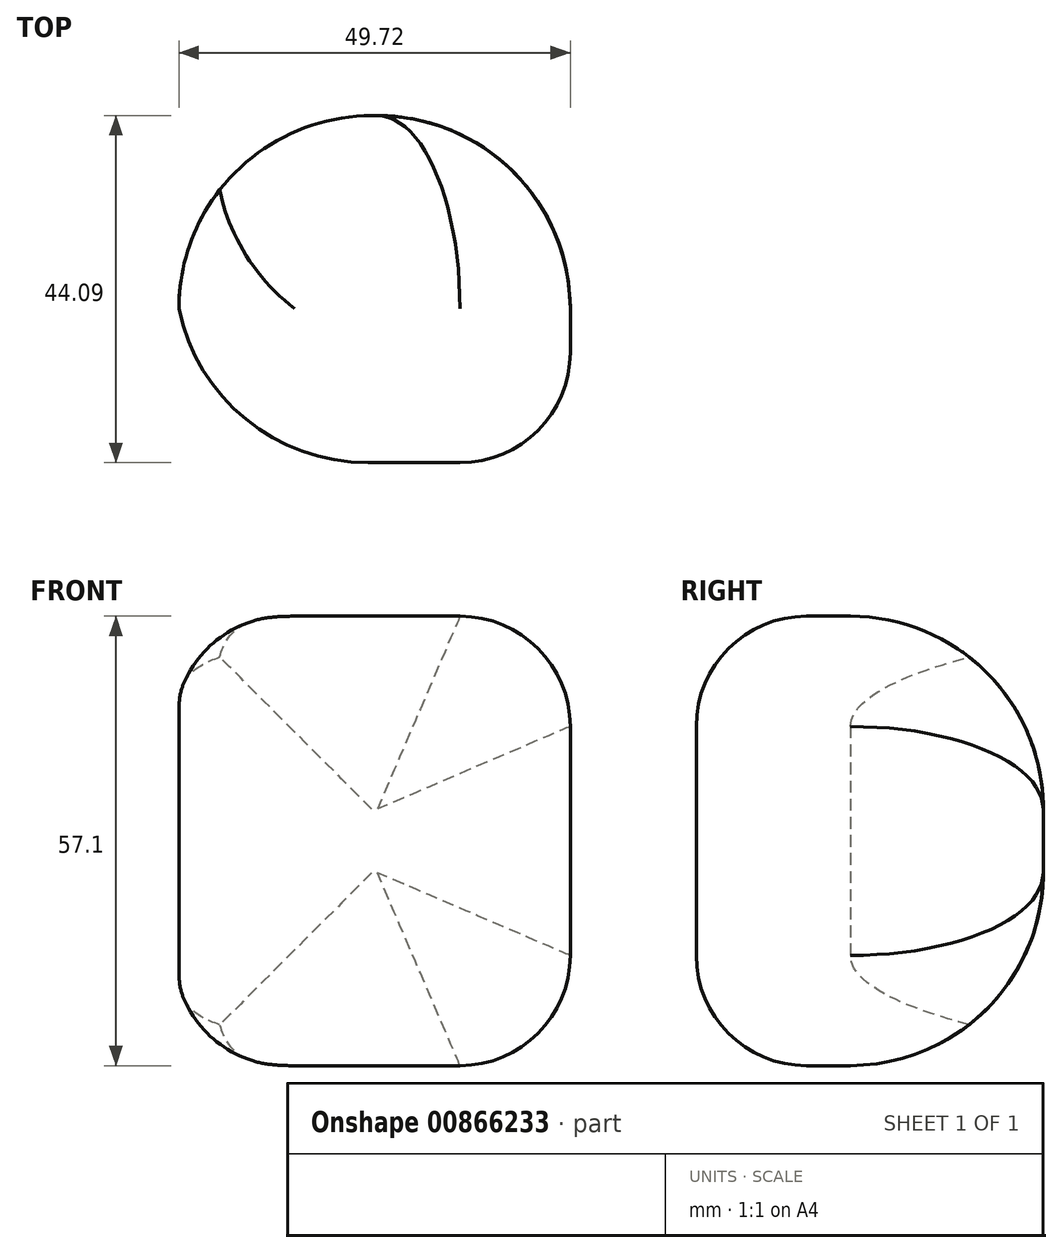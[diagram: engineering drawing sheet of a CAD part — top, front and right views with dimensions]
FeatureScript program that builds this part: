
annotation { "Feature Type Name" : "Feature", "Feature Type Description" : "" }
export const myFeature = defineFeature(function(context is Context, id is Id, definition is map)
    precondition{}
    {
        {
            var Q0;
            Q0=qCreatedBy(makeId("Top.planeOp"),FACE);
            var sketch = newSketch(context, id + "F0", { "sketchPlane" : qUnion([Q0])});
            skLineSegment(sketch, "E0.bottom", {"start": v(-18.6, 14.97) * mm, "end": v(31.12, 14.97) * mm});
            skLineSegment(sketch, "E0.top", {"start": v(-18.6, -29.12) * mm, "end": v(31.12, -29.12) * mm});
            skLineSegment(sketch, "E0.left", {"start": v(-18.6, 14.97) * mm, "end": v(-18.6, -29.12) * mm});
            skLineSegment(sketch, "E0.right", {"start": v(31.12, 14.97) * mm, "end": v(31.12, -29.12) * mm});
            skSolve(sketch);
        }
        {
            var Q0;
            Q0=makeQuery(id+"F0.imprint","IMPRINT",FACE,{"disambiguationData":[TD([[makeQuery(id+"F0.imprint","IMPRINT",EDGE,{"derivedFrom":sQuery(id+"F0.wireOp",EDGE,"E0.bottom")}),-1.0]])]});
            extrude(context, id + "F1", {"entities" : qUnion([Q0]), "depth" : 57.1 * mm, "offsetDistance" : 25 * mm});
        }
        {
            var Q0;
            Q0=makeQuery(id+"F1.opExtrude","SWEPT_FACE",FACE,{"disambiguationData":[OSD([sQuery(id+"F0.wireOp",EDGE,"E0.bottom")])]});
            fillet(context, id + "F2", {"entities" : qUnion([Q0]), "radius" : 24.5 * mm, "tangentPropagation" : true, "allowEdgeOverflow" : false});
        }
        {
            var Q0;
            Q0=makeQuery(id+"F1.opExtrude","SWEPT_EDGE",EDGE,{"disambiguationData":[OSD([sQuery(id+"F0.wireOp",EDGE,"E0.top"),sQuery(id+"F0.wireOp",EDGE,"E0.left")])]});
            fillet(context, id + "F3", {"entities" : qUnion([Q0]), "radius" : 24.5 * mm, "tangentPropagation" : true, "allowEdgeOverflow" : false});
        }
        {
            var Q0;
            Q0=makeQuery(id+"F1.opExtrude","SWEPT_FACE",FACE,{"disambiguationData":[OSD([sQuery(id+"F0.wireOp",EDGE,"E0.right")])]});
            var Q1;
            Q1=makeQuery(id+"F1.opExtrude","SWEPT_FACE",FACE,{"disambiguationData":[OSD([sQuery(id+"F0.wireOp",EDGE,"E0.top")])]});
            fillet(context, id + "F4", {"entities" : qUnion([Q0, Q1]), "radius" : 14 * mm, "tangentPropagation" : true, "allowEdgeOverflow" : false});
        }
    });
